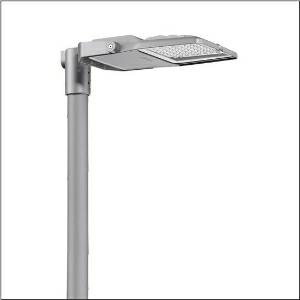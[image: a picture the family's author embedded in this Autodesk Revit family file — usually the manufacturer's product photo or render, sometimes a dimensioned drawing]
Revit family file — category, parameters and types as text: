
# Revit family: floodlight_fl_21_iq_mini___pl43_5xa7772d2a3a_1f0e
name_source: partatom
category: Lighting Fixtures
units: mm (PartAtom-declared; Revit-internal decimal feet)

## family parameters
Cut with Voids When Loaded = No
Host = Face
Light Source = No
Part Type = Normal
Room Calculation Point = No
Round Connector Dimension = Use Diameter
Shared = No

## types (1)
- --- (1 x LED, 18290 lm, 143 W, 3000K)
    Apparent Load = 143 VA
    CIE Flux Codes = 27 78 99 100 100
    Color Rendering = 70
    Color Temperature = 3000K
    Default Elevation = 1800 mm
    Description = Floodlight FL 21 iQ mini, floodlight, primary light control with lens, of PMMA, primary optical cover: protective disc, of toughened safety glass, transparent, light distribution: PL43, light emission: direct distribution, installation type: surface-mounted, LED, High Power LED, rated luminous flux: 18.290lm, luminous efficacy: 128lm/W, light colour: 730, colour temperature: 3000K, control gear: iQ Street-Remote/DALI, control: Auto-Match, Temp-Guard, Night-Set, Smart-Wire, Desk-Remote (wireless, voltage-free reading and setting of iQ features in the workshop via application-optimized NFC function/RFID function), optimised constant luminous flux control (CLO 2.0), Light-Fading, Lumen-Switch, with terminal, 6-pole, mains connection: 220..240V, AC, 50/60Hz, start of lifetime: 143W, end of service life: 152W, reduction: 61W, luminaire housing, of diecast aluminium, powder-coated, Siteco® metallic grey (DB 702S), corrosivity category C5 mid according to DIN EN ISO 12944, suitable for swimming pools, chlorine-resistant, sealing non-destructively replaceable, please order mast flange separately, mast bracket, of steel, galvanised, powder-coated, protection rating (complete): IP66, insulation class (complete): insulation class II (safety insulation), certification: CE, ENEC, VDE, protection symbol: D, impact resistance: IK08, permissible operating ambient temperature: -40..+40°C, permissible operating ambient temperature for outdoor applications: -40..+50°C, standard: DIN EN 12944, LABS conformity tested according to VDMA 24364:2018-05, packaging unit: 1 piece

Light Distribution: PL43
    Height = 70 mm
    Lamp = 1 x LED
    Lamp Light Flux = 18290 lm
    Lamp Power = 143 W
    Lamp count = 1
    Length = 485 mm
    Luminous efficacy = 128 lm/W
    Manufacturer = Siteco
    ModVariant = No
    Model = 5XA7772D2A3A
    Number of Poles = 1
    OnlyDefault = Yes
    Power Factor = 1
    Product Name = Floodlight FL 21 iQ mini | PL43
    Product group = floodlight | pylon annexe
    ProductGroupID = 6201
    Protection Class = Protection class II
    Protection Degree = IP 66
    RLX_Detail_Level = 1
    RLX_Emergency_Light_Flux = 0 lm
    RLX_Emergency_Type = 0
    RLX_Emergency_Type_DB = No
    RlxData = <blob elided: 101585 chars, md5=2cc1063c>
    Socket = socket
    Standby Power = 0 W
    System Light Flux = 18290 lm
    System Power = 143 W
    Type Comments = factory setting: luminous flux: 100 % | dim-lin: 254 | 730 mA
    Type Image = l_1007125.jpg
    URL = http://relux.com
    VarID = @adj_183073
    Voltage = 0 V
    Weight = 0.00 kg
    Width = 337 mm

## geometry (parser evidence)
native form markers: Blend x4, Sweep x13
no freeform markers — native parametric forms only
